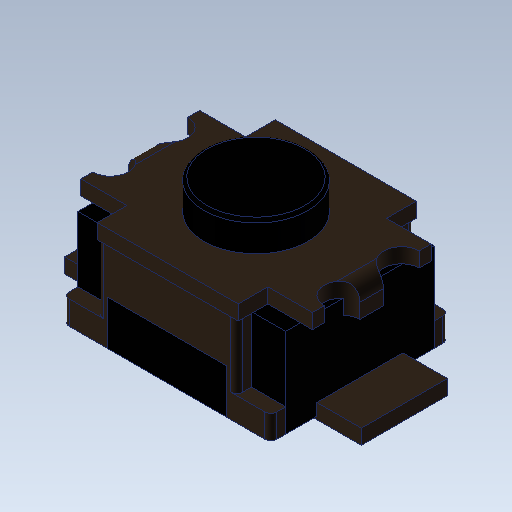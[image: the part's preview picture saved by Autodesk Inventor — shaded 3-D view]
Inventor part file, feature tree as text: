
AUTODESK INVENTOR PART (.ipt)
format: ipt  version: 2020 (Build 240168000, 168)  size: 182,272 bytes
history: native  units: in
note: dims shown in document units (in); Inventor stores cm internally (conversion verified against a paired STEP export)
features: fillet x2, mirror x1
ambient origin geometry x8: Origin, YZ Plane, XZ Plane, XY Plane, X Axis, Y Axis, Z Axis, Center Point
bodies: Solid1 (feature_tree), Solid2 (feature_tree), Solid3 (feature_tree)
feature tree (3):
  fillet  "Fillet2"  [1 undecoded]
  mirror  "Mirror3"
  fillet  "Fillet3"  [1 undecoded]
note: 2 required parameter values undecoded (feature->parameter linkage not recoverable at this tier; creation-order binding heuristic only, values carry confidence <= 0.55)
